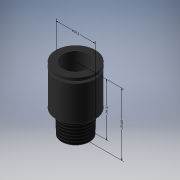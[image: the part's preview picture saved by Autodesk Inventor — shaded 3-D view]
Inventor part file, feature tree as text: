
AUTODESK INVENTOR PART (.ipt)
format: ipt  version: 2024.3 (Build 283343000, 343)  size: 169,472 bytes
history: native  units: mm
features: other x11, sketch x3, revolve x2, extrude x2, thread x1
ambient origin geometry x8: Origin, YZ Plane, XZ Plane, XY Plane, X Axis, Y Axis, Z Axis, Center Point
bodies: Solid1 (feature_tree)
feature tree (19):
  other  "Annotations"
  revolve  "Revolution1"  [1 undecoded]
  thread  "Thread1"  [1 undecoded]
  extrude  "Extrusion1"  Depth=21.5mm TaperAngle=0.0deg
  revolve  "Revolution2"  [1 undecoded]
  extrude  "Extrusion2"  [1 undecoded]
  other  "CNS_SCREW_XY"
  other  "CNS_SCREW_YZ"
  other  "CNS_SCREW_ZX"
  other  "CNS_SCREW_X"
  other  "CNS_SCREW_Y"
  other  "CNS_SCREW_Z"
  other  "CNS_SCREW_Center"
  sketch  "Sketch_1"  dims[d0=360.0deg d1=11.8158mm d2=0.0mm d3=26.314mm d4=0.0mm]
  sketch  "Sketch_2"  dims[d5=360.0deg d6=21.5mm d7=0.0mm]
  sketch  "Sketch_3"  dims[d10=18.2mm d8=24.3mm d9=29.0mm]
  other  "Linear Dimension 1"
  other  "Linear Dimension 2"
  other  "Linear Dimension 3"
note: 4 required parameter values undecoded (feature->parameter linkage not recoverable at this tier; creation-order binding heuristic only, values carry confidence <= 0.55)